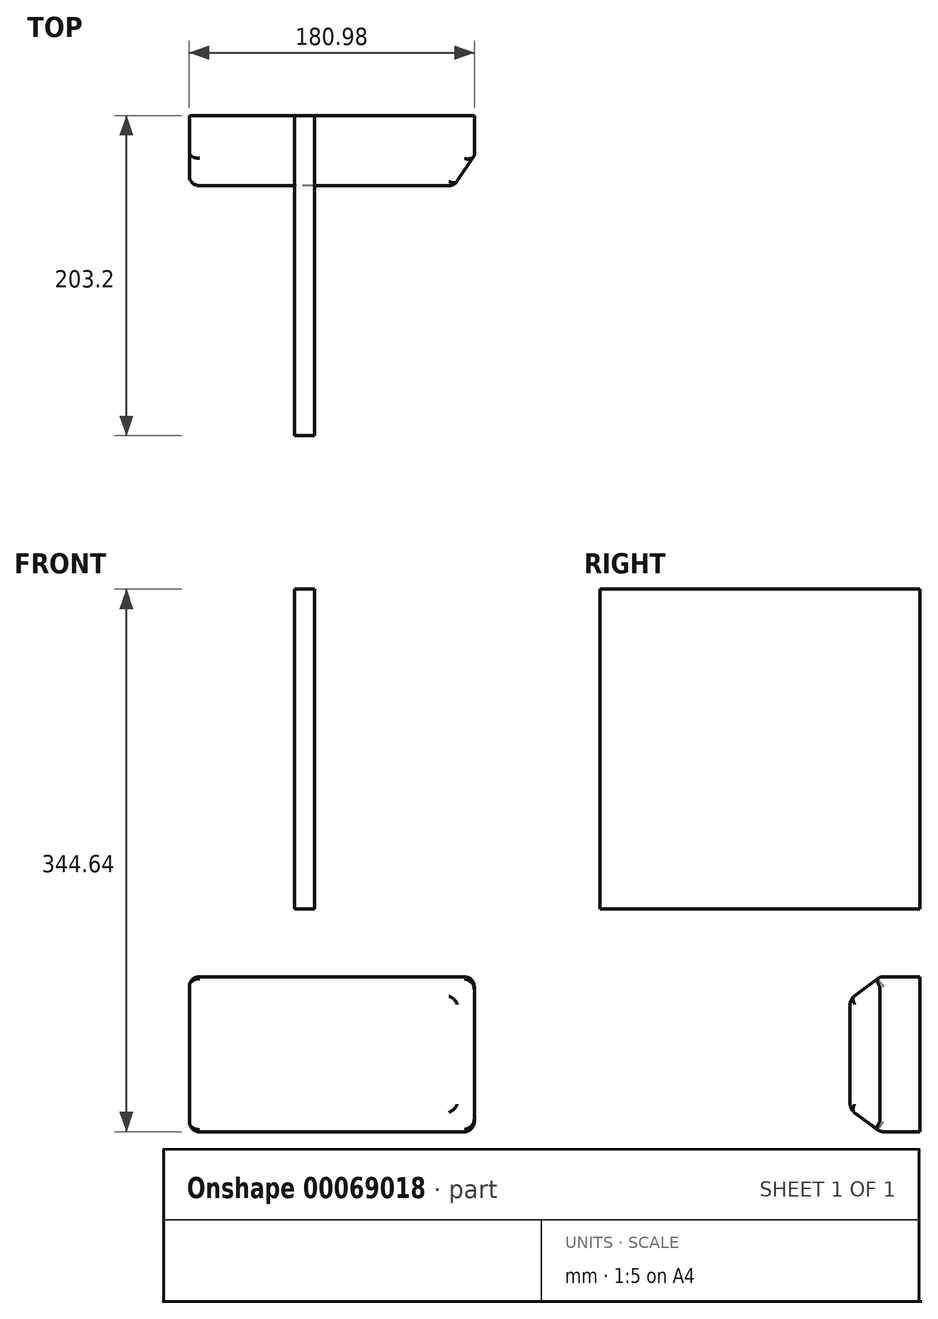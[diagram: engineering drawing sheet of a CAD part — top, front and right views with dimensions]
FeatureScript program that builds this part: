
annotation { "Feature Type Name" : "Feature", "Feature Type Description" : "" }
export const myFeature = defineFeature(function(context is Context, id is Id, definition is map)
    precondition{}
    {
        {
            var Q0;
            Q0=qCreatedBy(makeId("Front.planeOp"),FACE);
            var sketch = newSketch(context, id + "F0", { "sketchPlane" : qUnion([Q0])});
            skLineSegment(sketch, "E0.bottom", {"start": v(-66.84, 42.43) * mm, "end": v(114.14, 42.43) * mm});
            skLineSegment(sketch, "E0.top", {"start": v(-66.84, -56) * mm, "end": v(114.14, -56) * mm});
            skLineSegment(sketch, "E0.left", {"start": v(-66.84, 42.43) * mm, "end": v(-66.84, -56) * mm});
            skLineSegment(sketch, "E0.right", {"start": v(114.14, 42.43) * mm, "end": v(114.14, -56) * mm});
            skSolve(sketch);
        }
        {
            var Q0;
            Q0=makeQuery(id+"F0.imprint","IMPRINT",FACE,{"disambiguationData":[TD([[makeQuery(id+"F0.imprint","IMPRINT",EDGE,{"derivedFrom":sQuery(id+"F0.wireOp",EDGE,"E0.bottom")}),-1.0]])]});
            extrude(context, id + "F1", {"entities" : qUnion([Q0]), "depth" : 44.45 * mm});
        }
        {
            var Q0;
            Q0=makeQuery(id+"F1.opExtrude","SWEPT_FACE",FACE,{"disambiguationData":[OSD([sQuery(id+"F0.wireOp",EDGE,"E0.left")])]});
            var sketch = newSketch(context, id + "F2", { "sketchPlane" : qUnion([Q0])});
            skLineSegment(sketch, "E1.0", {"start": v(44.45, 42.43) * mm, "end": v(44.45, -56) * mm});
            skLineSegment(sketch, "E1.1", {"start": v(44.45, 42.43) * mm, "end": v(0, 42.43) * mm});
            skLineSegment(sketch, "E1.2", {"start": v(0, 42.43) * mm, "end": v(0, -56) * mm});
            skLineSegment(sketch, "E1.3", {"start": v(44.45, -56) * mm, "end": v(0, -56) * mm});
            skLineSegment(sketch, "E2", {"start": v(25.4, 42.43) * mm, "end": v(25.4, -56) * mm});
            skLineSegment(sketch, "E3", {"start": v(44.45, 28.14) * mm, "end": v(44.45, -41.7) * mm});
            skLineSegment(sketch, "E4", {"start": v(44.45, 28.14) * mm, "end": v(25.4, 42.43) * mm});
            skLineSegment(sketch, "E5", {"start": v(44.45, -41.7) * mm, "end": v(25.4, -56) * mm});
            skSolve(sketch);
        }
        {
            var Q0;
            {var subQ3=sQuery(id+"F2.wireOp",EDGE,"E4");Q0=makeQuery(id+"F2.imprint","IMPRINT",FACE,{"disambiguationData":[TD([[makeQuery(id+"F2.imprint","IMPRINT",EDGE,{"derivedFrom":subQ3}),-1.0]])]});}
            var Q1;
            {var subQ3=sQuery(id+"F2.wireOp",EDGE,"E5");Q1=makeQuery(id+"F2.imprint","IMPRINT",FACE,{"disambiguationData":[TD([[makeQuery(id+"F2.imprint","IMPRINT",EDGE,{"derivedFrom":subQ3}),1.0]])]});}
            extrude(context, id + "F3", {"entities" : qUnion([Q0, Q1]), "operationType" : NewBodyOperationType.REMOVE, "endBound" : BoundingType.THROUGH_ALL, "oppositeDirection" : true, "depth" : 25.4 * mm});
        }
        {
            var Q0;
            Q0=makeQuery(id+"F1.opExtrude","SWEPT_FACE",FACE,{"disambiguationData":[OSD([sQuery(id+"F0.wireOp",EDGE,"E0.bottom")])]});
            var sketch = newSketch(context, id + "F4", { "sketchPlane" : qUnion([Q0])});
            skLineSegment(sketch, "E6.0", {"start": v(114.14, -25.4) * mm, "end": v(114.14, 0) * mm});
            skLineSegment(sketch, "E6.1", {"start": v(114.14, -25.4) * mm, "end": v(-66.84, -25.4) * mm});
            skLineSegment(sketch, "E6.2", {"start": v(114.14, -44.45) * mm, "end": v(-66.84, -44.45) * mm});
            skLineSegment(sketch, "E6.3", {"start": v(114.14, -25.4) * mm, "end": v(114.14, -44.45) * mm});
            skLineSegment(sketch, "E7", {"start": v(114.14, -25.4) * mm, "end": v(101.44, -44.45) * mm});
            skSolve(sketch);
        }
        {
            var Q0;
            {var subQ0=sQuery(id+"F4.wireOp",EDGE,"E6.3");Q0=makeQuery(id+"F4.imprint","IMPRINT",FACE,{"disambiguationData":[TD([[makeQuery(id+"F4.imprint","IMPRINT",EDGE,{"derivedFrom":subQ0}),-1.0]])]});}
            extrude(context, id + "F5", {"entities" : qUnion([Q0]), "operationType" : NewBodyOperationType.REMOVE, "endBound" : BoundingType.THROUGH_ALL, "oppositeDirection" : true, "depth" : 25.4 * mm});
        }
        {
            var Q0;
            Q0=makeQuery(id+"F1.opExtrude","CAP_FACE",FACE,{"disambiguationData":[OSD([sQuery(id+"F0.wireOp",EDGE,"E0.bottom"),sQuery(id+"F0.wireOp",EDGE,"E0.top"),sQuery(id+"F0.wireOp",EDGE,"E0.left"),sQuery(id+"F0.wireOp",EDGE,"E0.right")])],"isStart":false});
            var Q1;
            Q1=makeQuery(id+"F3.boolean.opBoolean","COPY",FACE,{"derivedFrom":makeQuery(id+"F3.opExtrude","SWEPT_FACE",FACE,{"disambiguationData":[OSD([sQuery(id+"F2.wireOp",EDGE,"E4")])]})});
            var Q2;
            Q2=makeQuery(id+"F3.boolean.opBoolean","COPY",FACE,{"derivedFrom":makeQuery(id+"F3.opExtrude","SWEPT_FACE",FACE,{"disambiguationData":[OSD([sQuery(id+"F2.wireOp",EDGE,"E5")])]})});
            fillet(context, id + "F6", {"entities" : qUnion([Q0, Q1, Q2]), "radius" : 6.35 * mm, "tangentPropagation" : true, "allowEdgeOverflow" : false});
        }
        {
            var Q0;
            Q0=makeQuery(id+"F1.opExtrude","SWEPT_EDGE",EDGE,{"disambiguationData":[OSD([sQuery(id+"F0.wireOp",EDGE,"E0.bottom"),sQuery(id+"F0.wireOp",EDGE,"E0.left")])]});
            var Q1;
            Q1=makeQuery(id+"F1.opExtrude","SWEPT_EDGE",EDGE,{"disambiguationData":[OSD([sQuery(id+"F0.wireOp",EDGE,"E0.top"),sQuery(id+"F0.wireOp",EDGE,"E0.left")])]});
            var Q2;
            Q2=makeQuery(id+"F1.opExtrude","SWEPT_EDGE",EDGE,{"disambiguationData":[OSD([sQuery(id+"F0.wireOp",EDGE,"E0.top"),sQuery(id+"F0.wireOp",EDGE,"E0.right")])]});
            var Q3;
            Q3=makeQuery(id+"F5.boolean.opBoolean","COPY",EDGE,{"derivedFrom":makeQuery(id+"F5.opExtrude","SWEPT_EDGE",EDGE,{"disambiguationData":[OSD([sQuery(id+"F4.wireOp",EDGE,"E6.0"),sQuery(id+"F4.wireOp",EDGE,"E6.1"),sQuery(id+"F4.wireOp",EDGE,"E6.3"),sQuery(id+"F4.wireOp",EDGE,"E7")])]})});
            var Q4;
            Q4=makeQuery(id+"F1.opExtrude","SWEPT_EDGE",EDGE,{"disambiguationData":[OSD([sQuery(id+"F0.wireOp",EDGE,"E0.bottom"),sQuery(id+"F0.wireOp",EDGE,"E0.right")])]});
            fillet(context, id + "F7", {"entities" : qUnion([Q0, Q1, Q2, Q3, Q4]), "radius" : 6.35 * mm, "tangentPropagation" : true, "allowEdgeOverflow" : false});
        }
        {
            var Q0;
            Q0=qCreatedBy(makeId("Right.planeOp"),FACE);
            var sketch = newSketch(context, id + "F8", { "sketchPlane" : qUnion([Q0])});
            skLineSegment(sketch, "E8.bottom", {"start": v(-203.2, 85.45) * mm, "end": v(0, 85.45) * mm});
            skLineSegment(sketch, "E8.top", {"start": v(-203.2, 288.65) * mm, "end": v(0, 288.65) * mm});
            skLineSegment(sketch, "E8.left", {"start": v(-203.2, 85.45) * mm, "end": v(-203.2, 288.65) * mm});
            skLineSegment(sketch, "E8.right", {"start": v(0, 85.45) * mm, "end": v(0, 288.65) * mm});
            skSolve(sketch);
        }
        {
            var Q0;
            Q0=makeQuery(id+"F8.imprint","IMPRINT",FACE,{"disambiguationData":[TD([[makeQuery(id+"F8.imprint","IMPRINT",EDGE,{"derivedFrom":sQuery(id+"F8.wireOp",EDGE,"E8.bottom")}),1.0]])]});
            extrude(context, id + "F9", {"entities" : qUnion([Q0]), "depth" : 12.7 * mm});
        }
    });
